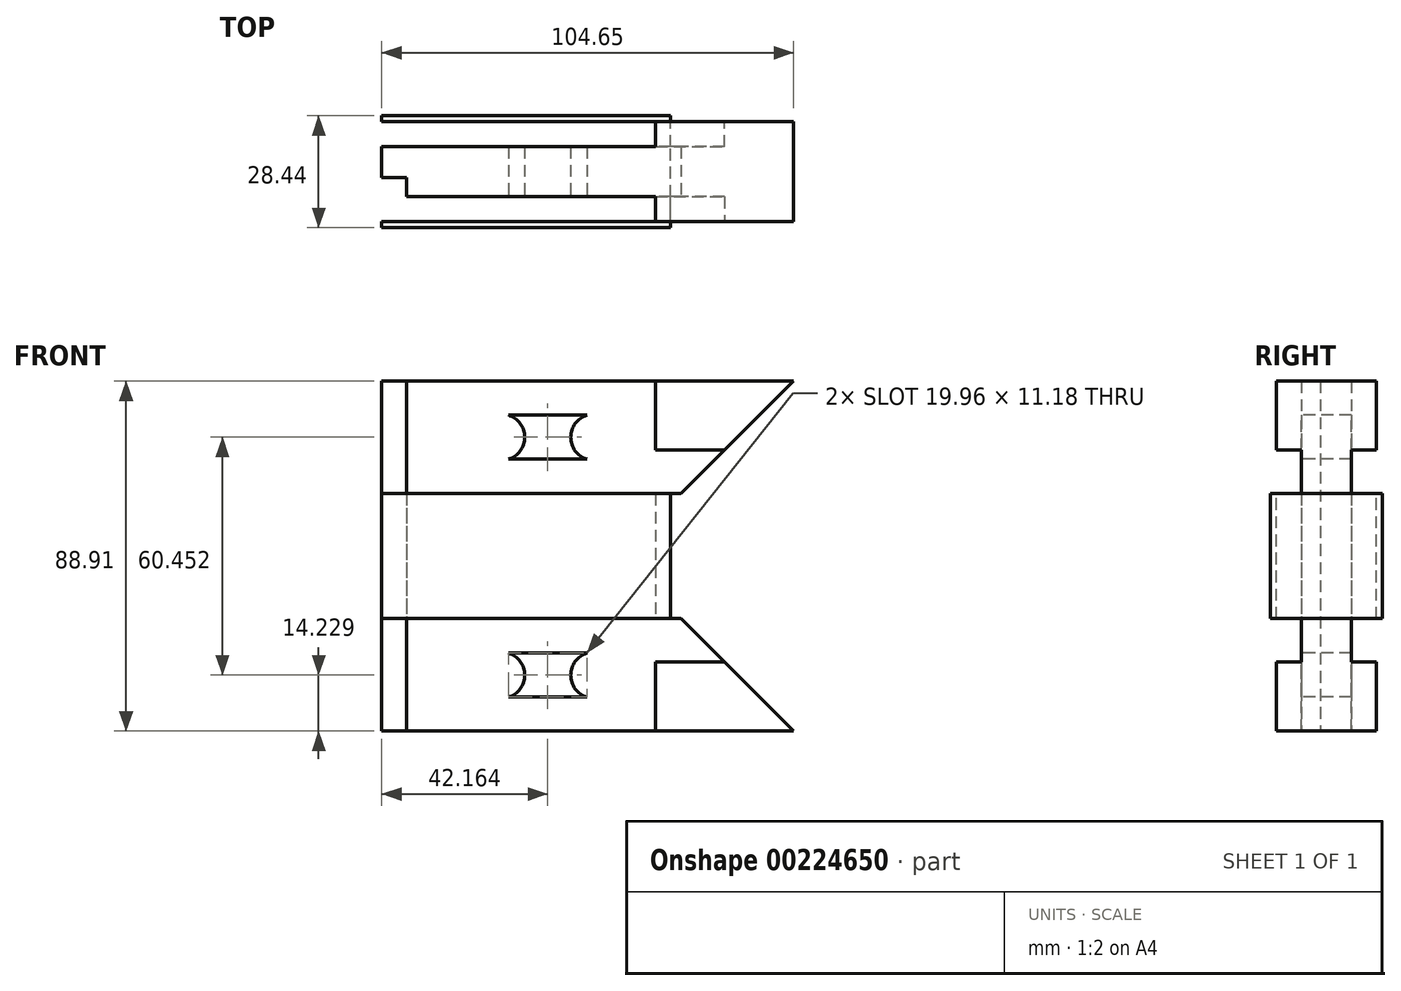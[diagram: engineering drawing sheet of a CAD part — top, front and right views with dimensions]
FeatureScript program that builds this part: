
annotation { "Feature Type Name" : "Feature", "Feature Type Description" : "" }
export const myFeature = defineFeature(function(context is Context, id is Id, definition is map)
    precondition{}
    {
        {
            var Q0;
            Q0=qCreatedBy(makeId("Top.planeOp"),FACE);
            var sketch = newSketch(context, id + "F0", { "sketchPlane" : qUnion([Q0])});
            skLineSegment(sketch, "E0", {"start": v(0, 0) * mm, "end": v(73.4, 0) * mm});
            skLineSegment(sketch, "E1", {"start": v(73.4, 0) * mm, "end": v(73.4, 14.22) * mm});
            skLineSegment(sketch, "E2", {"start": v(73.4, 14.22) * mm, "end": v(0, 14.22) * mm});
            skLineSegment(sketch, "E3", {"start": v(0, 14.22) * mm, "end": v(0, 0) * mm});
            skLineSegment(sketch, "E4", {"start": v(73.4, 0) * mm, "end": v(73.4, -14.22) * mm});
            skLineSegment(sketch, "E5", {"start": v(73.4, -14.22) * mm, "end": v(0, -14.22) * mm});
            skLineSegment(sketch, "E6", {"start": v(0, -14.22) * mm, "end": v(0, 0) * mm});
            skLineSegment(sketch, "E7", {"start": v(0, 0) * mm, "end": v(104.65, 0) * mm});
            skLineSegment(sketch, "E8", {"start": v(104.65, 0) * mm, "end": v(104.65, 12.7) * mm});
            skLineSegment(sketch, "E9", {"start": v(104.65, 12.7) * mm, "end": v(0, 12.7) * mm});
            skLineSegment(sketch, "E10", {"start": v(104.65, 0) * mm, "end": v(104.65, -12.7) * mm});
            skLineSegment(sketch, "E11", {"start": v(104.65, -12.7) * mm, "end": v(0, -12.7) * mm});
            skLineSegment(sketch, "E12", {"start": v(0, 12.7) * mm, "end": v(69.6, 12.7) * mm});
            skLineSegment(sketch, "E13", {"start": v(0, -12.7) * mm, "end": v(69.6, -12.7) * mm});
            skLineSegment(sketch, "E14", {"start": v(69.6, 12.7) * mm, "end": v(69.6, 6.35) * mm});
            skLineSegment(sketch, "E15", {"start": v(69.6, 6.35) * mm, "end": v(0, 6.35) * mm});
            skLineSegment(sketch, "E16", {"start": v(69.6, -12.7) * mm, "end": v(69.6, -6.35) * mm});
            skLineSegment(sketch, "E17", {"start": v(69.6, -6.35) * mm, "end": v(6.35, -6.35) * mm});
            skLineSegment(sketch, "E18", {"start": v(0, -6.35) * mm, "end": v(0, -1.52) * mm});
            skLineSegment(sketch, "E19", {"start": v(0, -1.52) * mm, "end": v(6.35, -1.52) * mm});
            skLineSegment(sketch, "E20", {"start": v(6.35, -1.52) * mm, "end": v(6.35, -6.35) * mm});
            skSolve(sketch);
        }
        {
            var Q0;
            {var subQ5=sQuery(id+"F0.wireOp",EDGE,"E8");Q0=makeQuery(id+"F0.imprint","IMPRINT",FACE,{"disambiguationData":[TD([[makeQuery(id+"F0.imprint","IMPRINT",EDGE,{"derivedFrom":subQ5}),1.0]])]});}
            var Q1;
            {var subQ5=sQuery(id+"F0.wireOp",EDGE,"E10");Q1=makeQuery(id+"F0.imprint","IMPRINT",FACE,{"disambiguationData":[TD([[makeQuery(id+"F0.imprint","IMPRINT",EDGE,{"derivedFrom":subQ5}),-1.0]])]});}
            var Q2;
            {var subQ6=sQuery(id+"F0.wireOp",EDGE,"E16");Q2=makeQuery(id+"F0.imprint","IMPRINT",FACE,{"disambiguationData":[TD([[makeQuery(id+"F0.imprint","IMPRINT",EDGE,{"derivedFrom":subQ6}),-1.0]])]});}
            var Q3;
            {var subQ6=sQuery(id+"F0.wireOp",EDGE,"E14");Q3=makeQuery(id+"F0.imprint","IMPRINT",FACE,{"disambiguationData":[TD([[makeQuery(id+"F0.imprint","IMPRINT",EDGE,{"derivedFrom":subQ6}),1.0]])]});}
            extrude(context, id + "F1", {"entities" : qUnion([Q0, Q1, Q2, Q3]), "depth" : 28.57 * mm});
        }
        {
            var Q0;
            {var subQ0=sQuery(id+"F0.wireOp",EDGE,"E12");Q0=makeQuery(id+"F0.imprint","IMPRINT",FACE,{"disambiguationData":[TD([[makeQuery(id+"F0.imprint","IMPRINT",EDGE,{"derivedFrom":subQ0}),-1.0]])]});}
            var Q1;
            {var subQ6=sQuery(id+"F0.wireOp",EDGE,"E14");Q1=makeQuery(id+"F0.imprint","IMPRINT",FACE,{"disambiguationData":[TD([[makeQuery(id+"F0.imprint","IMPRINT",EDGE,{"derivedFrom":subQ6}),1.0]])]});}
            var Q2;
            {var subQ6=sQuery(id+"F0.wireOp",EDGE,"E16");Q2=makeQuery(id+"F0.imprint","IMPRINT",FACE,{"disambiguationData":[TD([[makeQuery(id+"F0.imprint","IMPRINT",EDGE,{"derivedFrom":subQ6}),-1.0]])]});}
            var Q3;
            {var subQ0=sQuery(id+"F0.wireOp",EDGE,"E13");Q3=makeQuery(id+"F0.imprint","IMPRINT",FACE,{"disambiguationData":[TD([[makeQuery(id+"F0.imprint","IMPRINT",EDGE,{"derivedFrom":subQ0}),1.0]])]});}
            var Q4;
            {var subQ1=sQuery(id+"F0.wireOp",EDGE,"E5");Q4=makeQuery(id+"F0.imprint","IMPRINT",FACE,{"disambiguationData":[TD([[makeQuery(id+"F0.imprint","IMPRINT",EDGE,{"derivedFrom":subQ1}),-1.0]])]});}
            var Q5;
            {var subQ5=sQuery(id+"F0.wireOp",EDGE,"E2");Q5=makeQuery(id+"F0.imprint","IMPRINT",FACE,{"disambiguationData":[TD([[makeQuery(id+"F0.imprint","IMPRINT",EDGE,{"derivedFrom":subQ5}),1.0]])]});}
            extrude(context, id + "F2", {"entities" : qUnion([Q0, Q1, Q2, Q3, Q4, Q5]), "operationType" : NewBodyOperationType.ADD, "oppositeDirection" : true, "depth" : 15.88 * mm});
        }
        {
            var Q0;
            Q0=makeQuery(id+"F1.opExtrude","SWEPT_FACE",FACE,{"disambiguationData":[OSD([sQuery(id+"F0.wireOp",EDGE,"E11")])]});
            var sketch = newSketch(context, id + "F3", { "sketchPlane" : qUnion([Q0])});
            skLineSegment(sketch, "E21", {"start": v(104.65, 28.57) * mm, "end": v(71.99, -4.08) * mm});
            skSolve(sketch);
        }
        {
            var Q0;
            {var subQ1=sQuery(id+"F0.wireOp",EDGE,"E11");var subQ2=sQuery(id+"F0.wireOp",EDGE,"E10");var subQ3=makeQuery(id+"F1.opExtrude","SWEPT_EDGE",EDGE,{"disambiguationData":[OSD([subQ2,subQ1])]});Q0=makeQuery(id+"F3.imprint","IMPRINT",FACE,{"disambiguationData":[TD([[makeQuery(id+"F3.imprint","IMPRINT",EDGE,{"derivedFrom":subQ3}),-1.0]])]});}
            extrude(context, id + "F4", {"entities" : qUnion([Q0]), "operationType" : NewBodyOperationType.REMOVE, "endBound" : BoundingType.THROUGH_ALL, "oppositeDirection" : true, "depth" : 25.4 * mm});
        }
        {
            var Q0;
            Q0=makeQuery(id+"F1.opExtrude","SWEPT_FACE",FACE,{"disambiguationData":[OSD([sQuery(id+"F0.wireOp",EDGE,"E17")])]});
            var sketch = newSketch(context, id + "F5", { "sketchPlane" : qUnion([Q0])});
            skLineSegment(sketch, "E22", {"start": v(6.35, 28.58) * mm, "end": v(6.35, 14.35) * mm});
            skLineSegment(sketch, "E23", {"start": v(6.35, 14.35) * mm, "end": v(24.64, 14.35) * mm});
            skLineSegment(sketch, "E24", {"start": v(24.64, 14.35) * mm, "end": v(59.7, 14.35) * mm});
            skLineSegment(sketch, "E25.bottom", {"start": v(59.7, 19.94) * mm, "end": v(24.64, 19.94) * mm});
            skLineSegment(sketch, "E25.top", {"start": v(59.69, 8.76) * mm, "end": v(24.64, 8.76) * mm});
            skLineSegment(sketch, "E25.left", {"start": v(59.7, 19.94) * mm, "end": v(59.7, 8.76) * mm});
            skLineSegment(sketch, "E25.right", {"start": v(24.64, 19.94) * mm, "end": v(24.64, 8.76) * mm});
            skPoint(sketch, "E25.middle", {"position": v(42.16, 14.35) * mm});
            skLineSegment(sketch, "E26", {"start": v(24.64, 14.35) * mm, "end": v(30.48, 14.35) * mm});
            skLineSegment(sketch, "E27", {"start": v(59.7, 14.35) * mm, "end": v(53.85, 14.35) * mm});
            skArc(sketch, "E28", {"start": v(28.78, 19.94) * mm, "mid": v(24.64, 14.35) * mm, "end": v(28.78, 8.76) * mm});
            skArc(sketch, "E29", {"start": v(52.14, 19.94) * mm, "mid": v(48, 14.35) * mm, "end": v(52.14, 8.76) * mm});
            skArc(sketch, "E30.trimOffspring", {"start": v(32.18, 8.76) * mm, "mid": v(36.32, 14.35) * mm, "end": v(32.18, 19.94) * mm});
            skArc(sketch, "E31.trimOffspring", {"start": v(55.55, 8.76) * mm, "mid": v(59.7, 14.35) * mm, "end": v(55.55, 19.94) * mm});
            skSolve(sketch);
        }
        {
            var Q0;
            {var subQ1=sQuery(id+"F5.wireOp",EDGE,"E26");Q0=makeQuery(id+"F5.imprint","IMPRINT",FACE,{"disambiguationData":[TD([[makeQuery(id+"F5.imprint","IMPRINT",EDGE,{"derivedFrom":subQ1}),1.0]])]});}
            var Q1;
            {var subQ1=sQuery(id+"F5.wireOp",EDGE,"E26");Q1=makeQuery(id+"F5.imprint","IMPRINT",FACE,{"disambiguationData":[TD([[makeQuery(id+"F5.imprint","IMPRINT",EDGE,{"derivedFrom":subQ1}),-1.0]])]});}
            var Q2;
            {var subQ0=sQuery(id+"F5.wireOp",EDGE,"E30.trimOffspring");var subQ1=sQuery(id+"F5.wireOp",EDGE,"E24");var subQ2=makeQuery(id+"F5.imprint","INTERSECT",VERTEX,{"derivedFrom":[subQ1,subQ0]});Q2=makeQuery(id+"F5.imprint","IMPRINT",FACE,{"disambiguationData":[TD([[makeQuery(id+"F5.imprint","IMPRINT",EDGE,{"disambiguationData":[TD([[subQ2,-1.0]])],"derivedFrom":subQ1}),1.0]])]});}
            var Q3;
            {var subQ5=sQuery(id+"F5.wireOp",EDGE,"E27");Q3=makeQuery(id+"F5.imprint","IMPRINT",FACE,{"disambiguationData":[TD([[makeQuery(id+"F5.imprint","IMPRINT",EDGE,{"derivedFrom":subQ5}),-1.0]])]});}
            var Q4;
            {var subQ5=sQuery(id+"F5.wireOp",EDGE,"E27");Q4=makeQuery(id+"F5.imprint","IMPRINT",FACE,{"disambiguationData":[TD([[makeQuery(id+"F5.imprint","IMPRINT",EDGE,{"derivedFrom":subQ5}),1.0]])]});}
            var Q5;
            {var subQ0=sQuery(id+"F5.wireOp",EDGE,"E30.trimOffspring");var subQ1=sQuery(id+"F5.wireOp",EDGE,"E24");var subQ2=makeQuery(id+"F5.imprint","INTERSECT",VERTEX,{"derivedFrom":[subQ1,subQ0]});Q5=makeQuery(id+"F5.imprint","IMPRINT",FACE,{"disambiguationData":[TD([[makeQuery(id+"F5.imprint","IMPRINT",EDGE,{"disambiguationData":[TD([[subQ2,-1.0]])],"derivedFrom":subQ1}),-1.0]])]});}
            extrude(context, id + "F6", {"entities" : qUnion([Q0, Q1, Q2, Q3, Q4, Q5]), "operationType" : NewBodyOperationType.REMOVE, "endBound" : BoundingType.THROUGH_ALL, "oppositeDirection" : true, "depth" : 25.4 * mm});
        }
        {
            var Q0;
            Q0=makeQuery(id+"F1.opExtrude","SWEPT_FACE",FACE,{"disambiguationData":[OSD([sQuery(id+"F0.wireOp",EDGE,"E11")])]});
            var sketch = newSketch(context, id + "F7", { "sketchPlane" : qUnion([Q0])});
            skLineSegment(sketch, "E32", {"start": v(69.6, 28.58) * mm, "end": v(69.6, 11.05) * mm});
            skLineSegment(sketch, "E33", {"start": v(69.6, 11.05) * mm, "end": v(87.12, 11.05) * mm});
            skSolve(sketch);
        }
        {
            var Q0;
            Q0=makeQuery(id+"F1.opExtrude","SWEPT_FACE",FACE,{"disambiguationData":[OSD([sQuery(id+"F0.wireOp",EDGE,"E9")])]});
            var sketch = newSketch(context, id + "F8", { "sketchPlane" : qUnion([Q0])});
            skLineSegment(sketch, "E34", {"start": v(-69.6, 28.58) * mm, "end": v(-69.6, 11.05) * mm});
            skLineSegment(sketch, "E35", {"start": v(-69.6, 11.05) * mm, "end": v(-87.12, 11.05) * mm});
            skSolve(sketch);
        }
        {
            var Q0;
            {var subQ16=sQuery(id+"F8.wireOp",EDGE,"E35");Q0=makeQuery(id+"F8.imprint","IMPRINT",FACE,{"disambiguationData":[TD([[makeQuery(id+"F8.imprint","IMPRINT",EDGE,{"derivedFrom":subQ16}),1.0]])]});}
            extrude(context, id + "F9", {"entities" : qUnion([Q0]), "operationType" : NewBodyOperationType.REMOVE, "oppositeDirection" : true, "depth" : 6.35 * mm});
        }
        {
            var Q0;
            {var subQ16=sQuery(id+"F7.wireOp",EDGE,"E33");Q0=makeQuery(id+"F7.imprint","IMPRINT",FACE,{"disambiguationData":[TD([[makeQuery(id+"F7.imprint","IMPRINT",EDGE,{"derivedFrom":subQ16}),-1.0]])]});}
            extrude(context, id + "F10", {"entities" : qUnion([Q0]), "operationType" : NewBodyOperationType.REMOVE, "oppositeDirection" : true, "depth" : 6.35 * mm});
        }
        {
            var Q0;
            Q0=makeQuery(id+"F1.opExtrude","SWEPT_BODY",BODY,{"disambiguationData":[OSD([sQuery(id+"F0.wireOp",EDGE,"E3"),sQuery(id+"F0.wireOp",EDGE,"E6"),sQuery(id+"F0.wireOp",EDGE,"E8"),sQuery(id+"F0.wireOp",EDGE,"E9"),sQuery(id+"F0.wireOp",EDGE,"E10"),sQuery(id+"F0.wireOp",EDGE,"E11"),sQuery(id+"F0.wireOp",EDGE,"E14"),sQuery(id+"F0.wireOp",EDGE,"E15"),sQuery(id+"F0.wireOp",EDGE,"E16"),sQuery(id+"F0.wireOp",EDGE,"E17"),sQuery(id+"F0.wireOp",EDGE,"E19"),sQuery(id+"F0.wireOp",EDGE,"E20")])]});
            var Q1;
            Q1=makeQuery(id+"F2.opExtrude","CAP_FACE",FACE,{"disambiguationData":[OSD([sQuery(id+"F0.wireOp",EDGE,"E1"),sQuery(id+"F0.wireOp",EDGE,"E2"),sQuery(id+"F0.wireOp",EDGE,"E3"),sQuery(id+"F0.wireOp",EDGE,"E4"),sQuery(id+"F0.wireOp",EDGE,"E5"),sQuery(id+"F0.wireOp",EDGE,"E6"),sQuery(id+"F0.wireOp",EDGE,"E18")])],"isStart":false});
            mirror(context, id + "F11", {"operationType" : NewBodyOperationType.ADD, "entities" : qUnion([Q0]), "mirrorPlane" : qUnion([Q1])});
        }
    });
